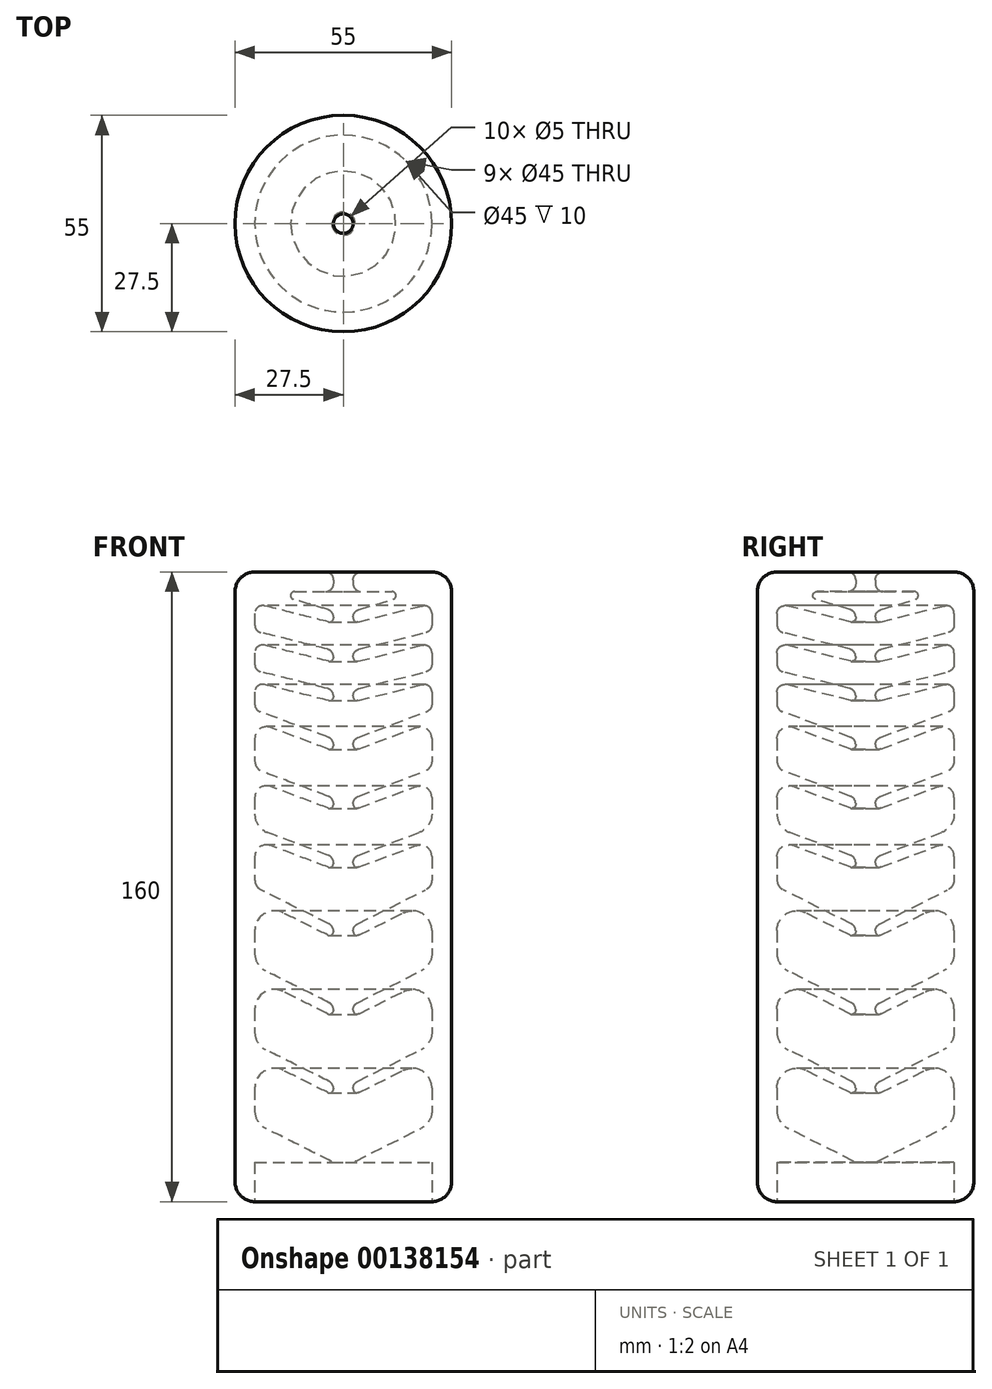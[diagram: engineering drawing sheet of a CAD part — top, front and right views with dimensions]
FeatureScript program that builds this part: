
annotation { "Feature Type Name" : "Feature", "Feature Type Description" : "" }
export const myFeature = defineFeature(function(context is Context, id is Id, definition is map)
    precondition{}
    {
        {
            var Q0;
            Q0=qCreatedBy(makeId("Front.planeOp"),FACE);
            var sketch = newSketch(context, id + "F0", { "sketchPlane" : qUnion([Q0]), "disableImprinting" : false});
            skLineSegment(sketch, "E0", {"start": v(0, 0) * mm, "end": v(0, 160) * mm});
            skPoint(sketch, "E1", {"position": v(2.5, 0) * mm});
            skPoint(sketch, "E2", {"position": v(22.5, 0) * mm});
            skPoint(sketch, "E3", {"position": v(27.5, 0) * mm});
            skLineSegment(sketch, "E4", {"start": v(27.5, 0) * mm, "end": v(27.5, 160) * mm});
            skLineSegment(sketch, "E5", {"start": v(22.5, 0) * mm, "end": v(27.5, 0) * mm});
            skLineSegment(sketch, "E6", {"start": v(2.5, 0) * mm, "end": v(2.5, 0) * mm});
            skPoint(sketch, "E7", {"position": v(2.5, 10) * mm});
            skLineSegment(sketch, "E8", {"start": v(3.6, 10.55) * mm, "end": v(19.74, 18.62) * mm});
            skLineSegment(sketch, "E9", {"start": v(3.6, 30.55) * mm, "end": v(19.74, 38.62) * mm});
            skLineSegment(sketch, "E10", {"start": v(3.6, 50.55) * mm, "end": v(19.74, 58.62) * mm});
            skLineSegment(sketch, "E11", {"start": v(3.6, 70.55) * mm, "end": v(20.84, 79.17) * mm});
            skLineSegment(sketch, "E12", {"start": v(3.8, 87.99) * mm, "end": v(19.26, 93.78) * mm});
            skLineSegment(sketch, "E13", {"start": v(3.8, 102.99) * mm, "end": v(20.55, 109.27) * mm});
            skLineSegment(sketch, "E14", {"start": v(3.8, 117.99) * mm, "end": v(21.2, 124.51) * mm});
            skLineSegment(sketch, "E15", {"start": v(4.01, 130.38) * mm, "end": v(20.99, 134.62) * mm});
            skLineSegment(sketch, "E16", {"start": v(4.01, 140.38) * mm, "end": v(20.99, 144.62) * mm});
            skLineSegment(sketch, "E17", {"start": v(3.93, 150.43) * mm, "end": v(12.68, 153.04) * mm});
            skLineSegment(sketch, "E18", {"start": v(4.5, 155) * mm, "end": v(12.4, 155) * mm});
            skLineSegment(sketch, "E19", {"start": v(24.5, 160) * mm, "end": v(4.5, 160) * mm});
            skLineSegment(sketch, "E20", {"start": v(24.5, 160) * mm, "end": v(27.5, 160) * mm});
            skLineSegment(sketch, "E21", {"start": v(3.95, 67.72) * mm, "end": v(15.26, 73.38) * mm});
            skLineSegment(sketch, "E22", {"start": v(3.95, 47.72) * mm, "end": v(15.26, 53.38) * mm});
            skLineSegment(sketch, "E23", {"start": v(3.95, 27.72) * mm, "end": v(15.26, 33.38) * mm});
            skLineSegment(sketch, "E24", {"start": v(3.85, 85) * mm, "end": v(18.45, 90.48) * mm});
            skLineSegment(sketch, "E25", {"start": v(3.85, 100) * mm, "end": v(18.45, 105.48) * mm});
            skLineSegment(sketch, "E26", {"start": v(3.85, 115) * mm, "end": v(18.45, 120.48) * mm});
            skLineSegment(sketch, "E27", {"start": v(3.74, 127.31) * mm, "end": v(20.01, 131.38) * mm});
            skLineSegment(sketch, "E28", {"start": v(3.74, 137.31) * mm, "end": v(20.01, 141.38) * mm});
            skLineSegment(sketch, "E29", {"start": v(3.74, 147.31) * mm, "end": v(20.01, 151.38) * mm});
            skLineSegment(sketch, "E30", {"start": v(2.5, 158) * mm, "end": v(2.5, 157) * mm});
            skLineSegment(sketch, "E31", {"start": v(2.5, 148.51) * mm, "end": v(2.5, 148.28) * mm});
            skLineSegment(sketch, "E32", {"start": v(2.5, 138.44) * mm, "end": v(2.5, 138.28) * mm});
            skLineSegment(sketch, "E33", {"start": v(2.5, 128.44) * mm, "end": v(2.5, 128.28) * mm});
            skLineSegment(sketch, "E34", {"start": v(2.5, 116.11) * mm, "end": v(2.5, 115.94) * mm});
            skLineSegment(sketch, "E35", {"start": v(2.5, 101.11) * mm, "end": v(2.5, 100.94) * mm});
            skLineSegment(sketch, "E36", {"start": v(2.5, 86.11) * mm, "end": v(2.5, 85.94) * mm});
            skLineSegment(sketch, "E37", {"start": v(2.5, 68.76) * mm, "end": v(2.5, 68.62) * mm});
            skLineSegment(sketch, "E38", {"start": v(2.5, 48.76) * mm, "end": v(2.5, 48.62) * mm});
            skLineSegment(sketch, "E39", {"start": v(2.5, 28.76) * mm, "end": v(2.5, 28.62) * mm});
            skLineSegment(sketch, "E40", {"start": v(22.5, 149.44) * mm, "end": v(22.5, 146.56) * mm});
            skLineSegment(sketch, "E41", {"start": v(22.5, 139.44) * mm, "end": v(22.5, 136.56) * mm});
            skLineSegment(sketch, "E42", {"start": v(22.5, 129.44) * mm, "end": v(22.5, 126.39) * mm});
            skLineSegment(sketch, "E43", {"start": v(22.5, 117.67) * mm, "end": v(22.5, 112.08) * mm});
            skLineSegment(sketch, "E44", {"start": v(22.5, 102.67) * mm, "end": v(22.5, 98.47) * mm});
            skLineSegment(sketch, "E45", {"start": v(22.5, 87.67) * mm, "end": v(22.5, 81.85) * mm});
            skLineSegment(sketch, "E46", {"start": v(22.5, 68.9) * mm, "end": v(22.5, 63.1) * mm});
            skLineSegment(sketch, "E47", {"start": v(22.5, 48.9) * mm, "end": v(22.5, 43.1) * mm});
            skLineSegment(sketch, "E48", {"start": v(22.5, 28.9) * mm, "end": v(22.5, 23.1) * mm});
            skLineSegment(sketch, "E49", {"start": v(22.5, 10) * mm, "end": v(22.5, 0) * mm});
            skArc(sketch, "E50.filletArc", {"start": v(19.74, 18.62) * mm, "mid": v(21.75, 20.46) * mm, "end": v(22.5, 23.1) * mm});
            skArc(sketch, "E51.filletArc", {"start": v(22.5, 28.9) * mm, "mid": v(20.13, 33.16) * mm, "end": v(15.26, 33.38) * mm});
            skArc(sketch, "E52.filletArc", {"start": v(22.5, 48.9) * mm, "mid": v(20.13, 53.16) * mm, "end": v(15.26, 53.38) * mm});
            skArc(sketch, "E53.filletArc", {"start": v(19.74, 38.62) * mm, "mid": v(21.75, 40.46) * mm, "end": v(22.5, 43.1) * mm});
            skArc(sketch, "E54.filletArc", {"start": v(19.74, 58.62) * mm, "mid": v(21.75, 60.46) * mm, "end": v(22.5, 63.1) * mm});
            skArc(sketch, "E55.filletArc", {"start": v(22.5, 68.9) * mm, "mid": v(20.13, 73.16) * mm, "end": v(15.26, 73.38) * mm});
            skArc(sketch, "E56.filletArc", {"start": v(22.5, 87.67) * mm, "mid": v(21.2, 90.14) * mm, "end": v(18.45, 90.48) * mm});
            skArc(sketch, "E57.filletArc", {"start": v(20.84, 79.17) * mm, "mid": v(22.05, 80.28) * mm, "end": v(22.5, 81.85) * mm});
            skArc(sketch, "E58.filletArc", {"start": v(19.26, 93.78) * mm, "mid": v(21.6, 95.62) * mm, "end": v(22.5, 98.47) * mm});
            skArc(sketch, "E59.filletArc", {"start": v(22.5, 102.67) * mm, "mid": v(21.2, 105.14) * mm, "end": v(18.45, 105.48) * mm});
            skArc(sketch, "E60.filletArc", {"start": v(20.55, 109.27) * mm, "mid": v(21.97, 110.37) * mm, "end": v(22.5, 112.08) * mm});
            skArc(sketch, "E61.filletArc", {"start": v(22.5, 117.67) * mm, "mid": v(21.2, 120.14) * mm, "end": v(18.45, 120.48) * mm});
            skArc(sketch, "E62.filletArc", {"start": v(21.2, 124.51) * mm, "mid": v(22.14, 125.25) * mm, "end": v(22.5, 126.39) * mm});
            skArc(sketch, "E63.filletArc", {"start": v(22.5, 129.44) * mm, "mid": v(21.73, 131.01) * mm, "end": v(20.01, 131.38) * mm});
            skArc(sketch, "E64.filletArc", {"start": v(20.99, 134.62) * mm, "mid": v(22.08, 135.33) * mm, "end": v(22.5, 136.56) * mm});
            skArc(sketch, "E65.filletArc", {"start": v(22.5, 139.44) * mm, "mid": v(21.73, 141.01) * mm, "end": v(20.01, 141.38) * mm});
            skArc(sketch, "E66.filletArc", {"start": v(20.99, 144.62) * mm, "mid": v(22.08, 145.33) * mm, "end": v(22.5, 146.56) * mm});
            skArc(sketch, "E67.filletArc", {"start": v(22.5, 149.44) * mm, "mid": v(21.73, 151.01) * mm, "end": v(20.01, 151.38) * mm});
            skArc(sketch, "E68.filletArc", {"start": v(12.68, 153.04) * mm, "mid": v(13.38, 154.14) * mm, "end": v(12.4, 155) * mm});
            skArc(sketch, "E69.filletArc", {"start": v(3.93, 150.43) * mm, "mid": v(2.9, 149.7) * mm, "end": v(2.5, 148.51) * mm});
            skArc(sketch, "E70.filletArc", {"start": v(4.01, 140.38) * mm, "mid": v(2.92, 139.67) * mm, "end": v(2.5, 138.44) * mm});
            skArc(sketch, "E71.filletArc", {"start": v(4.01, 130.38) * mm, "mid": v(2.92, 129.67) * mm, "end": v(2.5, 128.44) * mm});
            skArc(sketch, "E72.filletArc", {"start": v(3.8, 117.99) * mm, "mid": v(2.86, 117.25) * mm, "end": v(2.5, 116.11) * mm});
            skArc(sketch, "E73.filletArc", {"start": v(3.8, 102.99) * mm, "mid": v(2.86, 102.25) * mm, "end": v(2.5, 101.11) * mm});
            skArc(sketch, "E74.filletArc", {"start": v(3.8, 87.99) * mm, "mid": v(2.86, 87.25) * mm, "end": v(2.5, 86.11) * mm});
            skArc(sketch, "E75.filletArc", {"start": v(3.6, 70.55) * mm, "mid": v(2.8, 69.82) * mm, "end": v(2.5, 68.76) * mm});
            skArc(sketch, "E76.filletArc", {"start": v(3.6, 50.55) * mm, "mid": v(2.8, 49.82) * mm, "end": v(2.5, 48.76) * mm});
            skArc(sketch, "E77.filletArc", {"start": v(3.6, 30.55) * mm, "mid": v(2.8, 29.82) * mm, "end": v(2.5, 28.76) * mm});
            skPoint(sketch, "E78.visualSharp", {"position": v(2.5, 160) * mm});
            skArc(sketch, "E78.filletArc", {"start": v(4.5, 160) * mm, "mid": v(3.09, 159.41) * mm, "end": v(2.5, 158) * mm});
            skArc(sketch, "E79.filletArc", {"start": v(2.5, 157) * mm, "mid": v(3.09, 155.59) * mm, "end": v(4.5, 155) * mm});
            skLineSegment(sketch, "E80", {"start": v(3.06, 10.28) * mm, "end": v(3.6, 10.55) * mm});
            skLineSegment(sketch, "E81", {"start": v(3.13, 10) * mm, "end": v(22.5, 10) * mm});
            skArc(sketch, "E82.filletArc", {"start": v(3.06, 10.28) * mm, "mid": v(2.98, 10.11) * mm, "end": v(3.13, 10) * mm});
            skArc(sketch, "E83.filletArc", {"start": v(2.5, 28.62) * mm, "mid": v(2.97, 27.77) * mm, "end": v(3.95, 27.72) * mm});
            skArc(sketch, "E84.filletArc", {"start": v(2.5, 48.62) * mm, "mid": v(2.97, 47.77) * mm, "end": v(3.95, 47.72) * mm});
            skArc(sketch, "E85.filletArc", {"start": v(2.5, 68.62) * mm, "mid": v(2.97, 67.77) * mm, "end": v(3.95, 67.72) * mm});
            skArc(sketch, "E86.filletArc", {"start": v(2.5, 85.94) * mm, "mid": v(2.93, 85.12) * mm, "end": v(3.85, 85) * mm});
            skArc(sketch, "E87.filletArc", {"start": v(2.5, 100.94) * mm, "mid": v(2.93, 100.12) * mm, "end": v(3.85, 100) * mm});
            skArc(sketch, "E88.filletArc", {"start": v(2.5, 115.94) * mm, "mid": v(2.93, 115.12) * mm, "end": v(3.85, 115) * mm});
            skArc(sketch, "E89.filletArc", {"start": v(2.5, 128.28) * mm, "mid": v(2.88, 127.5) * mm, "end": v(3.74, 127.31) * mm});
            skArc(sketch, "E90.filletArc", {"start": v(2.5, 138.28) * mm, "mid": v(2.88, 137.5) * mm, "end": v(3.74, 137.31) * mm});
            skArc(sketch, "E91.filletArc", {"start": v(2.5, 148.28) * mm, "mid": v(2.88, 147.5) * mm, "end": v(3.74, 147.31) * mm});
            skSolve(sketch);
        }
        {
            var Q0;
            Q0=makeQuery(id+"F0.imprint","IMPRINT",FACE,{"disambiguationData":[TD([[makeQuery(id+"F0.imprint","IMPRINT",EDGE,{"derivedFrom":sQuery(id+"F0.wireOp",EDGE,"E4")}),1.0]])]});
            var Q1;
            Q1=sQuery(id+"F0.wireOp",EDGE,"E0");
            revolve(context, id + "F1", {"entities" : qUnion([Q0]), "axis" : qUnion([Q1]), "revolveType" : RevolveType.FULL});
        }
        {
            var Q0;
            Q0=makeQuery(id+"F1.opRevolve","SWEPT_EDGE",EDGE,{"disambiguationData":[OSD([sQuery(id+"F0.wireOp",EDGE,"E4"),sQuery(id+"F0.wireOp",EDGE,"E20")])]});
            var Q1;
            Q1=makeQuery(id+"F1.opRevolve","SWEPT_EDGE",EDGE,{"disambiguationData":[OSD([sQuery(id+"F0.wireOp",EDGE,"E4"),sQuery(id+"F0.wireOp",EDGE,"E5")])]});
            fillet(context, id + "F2", {"entities" : qUnion([Q0, Q1]), "radius" : 5 * mm, "tangentPropagation" : true, "allowEdgeOverflow" : false});
        }
    });
